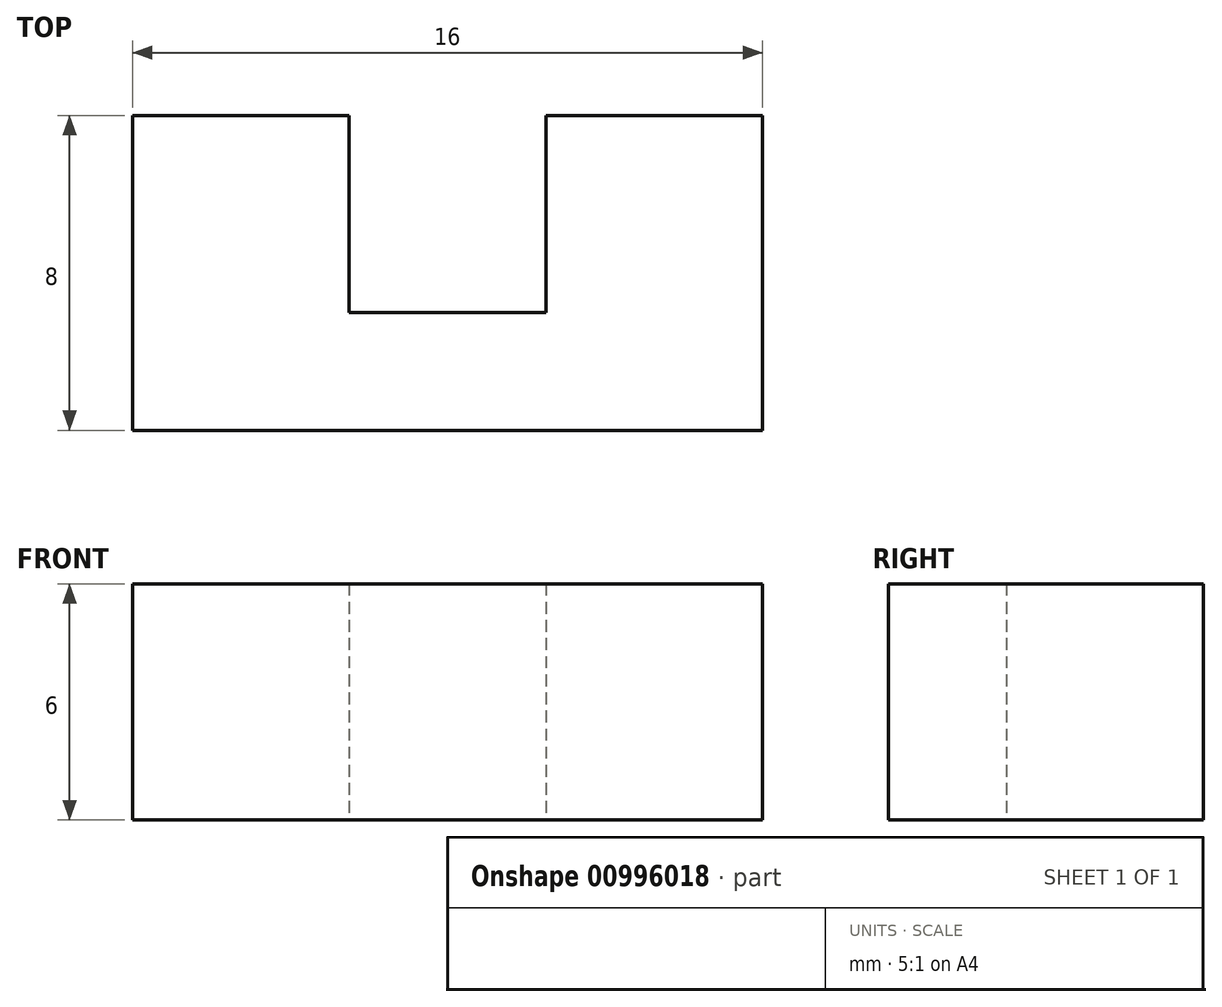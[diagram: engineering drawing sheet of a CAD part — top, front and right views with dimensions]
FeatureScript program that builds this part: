
annotation { "Feature Type Name" : "Feature", "Feature Type Description" : "" }
export const myFeature = defineFeature(function(context is Context, id is Id, definition is map)
    precondition{}
    {
        {
            var Q0;
            Q0=qCreatedBy(makeId("Top.planeOp"),FACE);
            var sketch = newSketch(context, id + "F0", { "sketchPlane" : qUnion([Q0])});
            skLineSegment(sketch, "E0.bottom", {"start": v(8, -4) * mm, "end": v(-8, -4) * mm});
            skLineSegment(sketch, "E0.top", {"start": v(8, 4) * mm, "end": v(-8, 4) * mm});
            skLineSegment(sketch, "E0.left", {"start": v(8, -4) * mm, "end": v(8, 4) * mm});
            skLineSegment(sketch, "E0.right", {"start": v(-8, -4) * mm, "end": v(-8, 4) * mm});
            skPoint(sketch, "E0.middle", {"position": v(0, 0) * mm});
            skLineSegment(sketch, "E1.bottom", {"start": v(0, 4) * mm, "end": v(2.5, 4) * mm});
            skLineSegment(sketch, "E1.top", {"start": v(0, -1) * mm, "end": v(2.5, -1) * mm});
            skLineSegment(sketch, "E1.left", {"start": v(0, 4) * mm, "end": v(0, -1) * mm});
            skLineSegment(sketch, "E1.right", {"start": v(2.5, 4) * mm, "end": v(2.5, -1) * mm});
            skLineSegment(sketch, "E2.MirrorCS", {"start": v(-2.5, 4) * mm, "end": v(-2.5, -1) * mm});
            skLineSegment(sketch, "E3.MirrorCS", {"start": v(0, -1) * mm, "end": v(-2.5, -1) * mm});
            skSolve(sketch);
        }
        {
            var Q0;
            Q0=makeQuery(id+"F0.imprint","IMPRINT",FACE,{"disambiguationData":[TD([[makeQuery(id+"F0.imprint","IMPRINT",EDGE,{"derivedFrom":sQuery(id+"F0.wireOp",EDGE,"E0.bottom")}),-1.0]])]});
            extrude(context, id + "F1", {"entities" : qUnion([Q0]), "depth" : 6 * mm, "offsetDistance" : 25 * mm});
        }
    });
